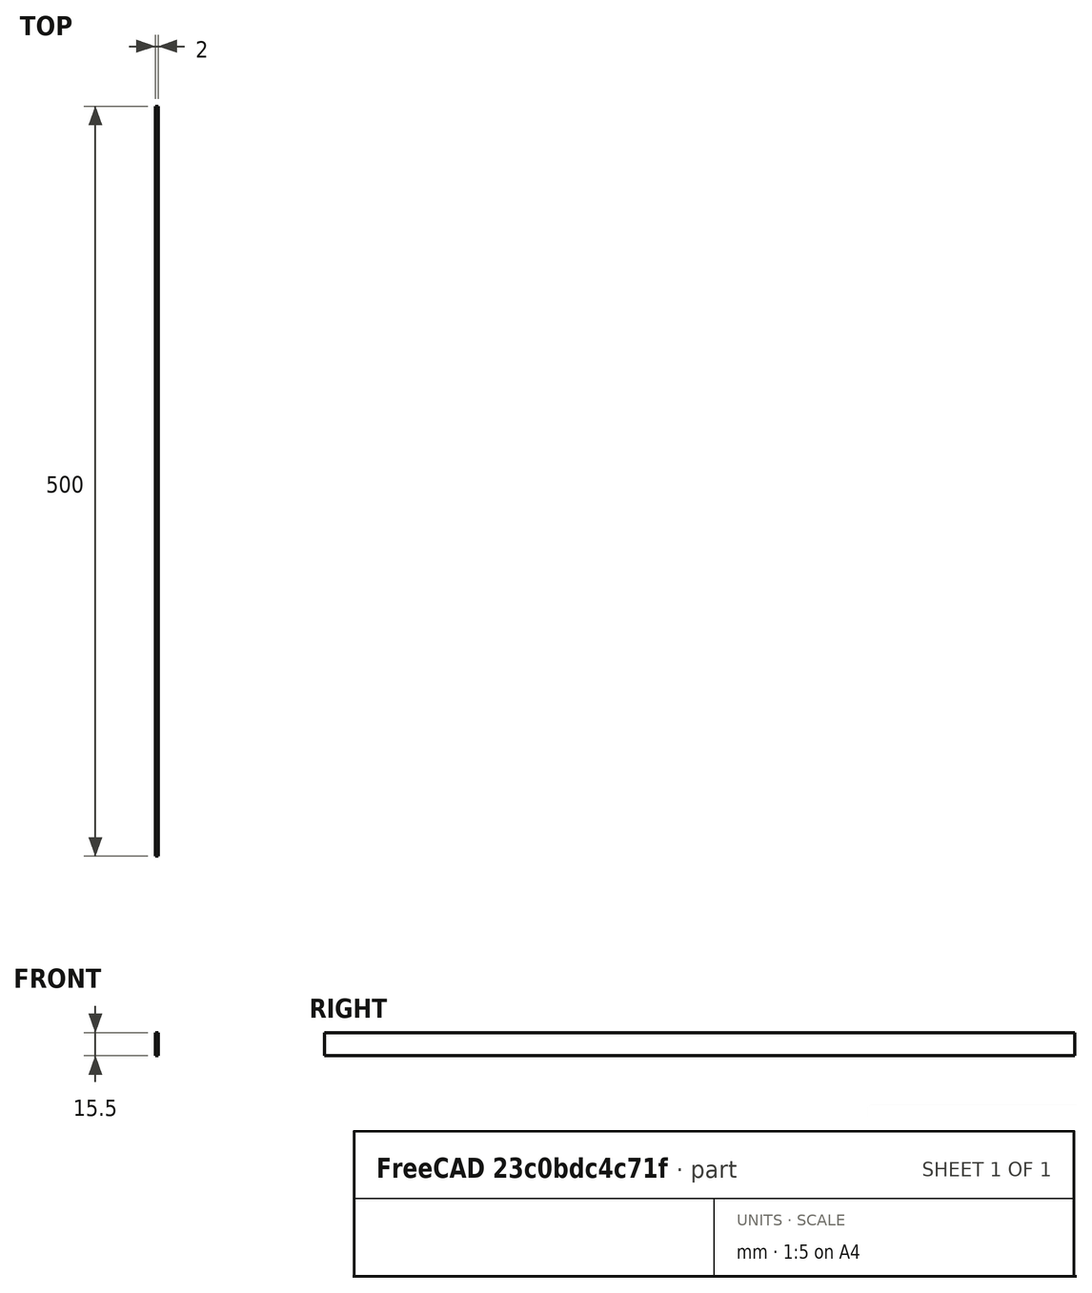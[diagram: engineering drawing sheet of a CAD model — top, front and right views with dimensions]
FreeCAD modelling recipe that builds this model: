
FCSTD DOCUMENT  (FreeCAD 0.19R24276 (Git))
Label: 1001_keaboard_tmould_19_
License: All rights reserved
LicenseURL: http://en.wikipedia.org/wiki/All_rights_reserved
objects: Spreadsheet::Sheet×1, Sketcher::SketchObject×1, PartDesign::Pad×1, PartDesign::Body×1
note: 4 computed .brp shape members not serialized (recipe doc carries the construction recipe); baked Part::Feature solids carry a one-line shape summary decoded from their .brp

FEATURE [Spreadsheet::Sheet] Spreadsheet  label="xls"
  cells = B3=T-Mould; G3=https://www.obi.ch/profile/combitech-flachstange-pvc-weiss-15-5-mm-x-1-m/p/3759164; B5=Width; C5=Profile_Width; D5(Profile_Width)=15.5; G5=Art.Nr. 3759164; H5=Combitech Flachstange PVC Weiss 15,5 mm x 1 m; B6=Thickness; C6=Profile_thickness; D6(Profile_thickness)=2
FEATURE [Sketcher::SketchObject] Sketch002
  FullyConstrained = true
  MapMode = 5
  Placement = pos=(0,0,0) rot=(1,0,0;1.5708rad)
  Support = -> [XZ_Plane]
  expr: Constraints[9] = <<xls>>.Profile_thickness
  expr: Constraints[10] = <<xls>>.Profile_Width
  sketch-geometry (4):
    g0: LineSegment StartX=0 StartY=15.5 StartZ=0 EndX=-2 EndY=15.5 EndZ=0
    g1: LineSegment StartX=-2 StartY=15.5 StartZ=0 EndX=-2 EndY=0 EndZ=0
    g2: LineSegment StartX=-2 StartY=0 StartZ=0 EndX=0 EndY=0 EndZ=0
    g3: LineSegment StartX=0 StartY=0 StartZ=0 EndX=0 EndY=15.5 EndZ=0
  constraints (11):
    c: Coincident(g0,g1)
    c: Coincident(g1,g2)
    c: Coincident(g2,g3)
    c: Coincident(g3,g0)
    c: Horizontal(g0)
    c: Horizontal(g2)
    c: Vertical(g1)
    c: Vertical(g3)
    c: Coincident(g2,g-1)
    c: DistanceX(g0,g0) = 2
    c: DistanceY(g1,g1) = 15.5
FEATURE [PartDesign::Pad] Pad
  AllowMultiFace = false
  Direction = (1,1,1)
  Length = 500
  Length2 = 100
  Placement = pos=(0,0,0) rot=(1,0,0;1.5708rad)
  Profile = -> Sketch002
  Reversed = true
  Type = 0
FEATURE [PartDesign::Body] Body
  Group = -> [Sketch002,Pad]
  Origin = -> Origin
  Tip = -> Pad
